FCSTD DOCUMENT  (FreeCAD 0.15R4671 (Git))
Label: plate
License: All rights reserved
LicenseURL: http://en.wikipedia.org/wiki/All_rights_reserved
objects: Sketcher::SketchObject×1
note: 1 computed .brp shape members not serialized (recipe doc carries the construction recipe); baked Part::Feature solids carry a one-line shape summary decoded from their .brp

FEATURE [Sketcher::SketchObject] Sketch
  sketch-geometry (29):
    g0: Circle [constr] CenterX=0 CenterY=0 CenterZ=0 NormalX=0 NormalY=0 NormalZ=1 Radius=72.75
    g1: Circle [constr] CenterX=0 CenterY=0 CenterZ=0 NormalX=0 NormalY=0 NormalZ=1 Radius=99.75
    g2: LineSegment [constr] StartX=-72.75 StartY=0 StartZ=0 EndX=-99.75 EndY=0 EndZ=0
    g3: Circle [constr] CenterX=0 CenterY=0 CenterZ=0 NormalX=0 NormalY=0 NormalZ=1 Radius=79.25
    g4: LineSegment [constr] StartX=72.75 StartY=0 StartZ=0 EndX=79.25 EndY=0 EndZ=0
    g5: Circle [constr] CenterX=0 CenterY=0 CenterZ=0 NormalX=0 NormalY=0 NormalZ=1 Radius=93.25
    g6: LineSegment [constr] StartX=93.25 StartY=0 StartZ=0 EndX=99.75 EndY=0 EndZ=0
    g7: LineSegment [constr] StartX=0 StartY=0 StartZ=0 EndX=0 EndY=200 EndZ=0
    g8: LineSegment [constr] StartX=0 StartY=0 StartZ=0 EndX=0 EndY=-200 EndZ=0
    g9: Circle CenterX=0 CenterY=93.25 CenterZ=0 NormalX=0 NormalY=0 NormalZ=1 Radius=4.75
    g10: Circle CenterX=93.25 CenterY=0 CenterZ=0 NormalX=0 NormalY=0 NormalZ=1 Radius=4.75
    g11: Circle CenterX=-93.25 CenterY=0 CenterZ=0 NormalX=0 NormalY=0 NormalZ=1 Radius=4.75
    g12: Circle CenterX=0 CenterY=-93.25 CenterZ=0 NormalX=0 NormalY=0 NormalZ=1 Radius=4.75
    g13: Circle CenterX=0 CenterY=0 CenterZ=0 NormalX=0 NormalY=0 NormalZ=1 Radius=102
    g14: Circle [constr] CenterX=0 CenterY=0 CenterZ=0 NormalX=0 NormalY=0 NormalZ=1 Radius=64.935
    g15: Circle [constr] CenterX=0 CenterY=40.745 CenterZ=0 NormalX=0 NormalY=0 NormalZ=1 Radius=24.19
    g16: Circle CenterX=0 CenterY=40.745 CenterZ=0 NormalX=0 NormalY=0 NormalZ=1 Radius=9
    g17: LineSegment [constr] StartX=-29.7982 StartY=48.145 StartZ=0 EndX=0 EndY=48.145 EndZ=0
    g18: Circle CenterX=-17.45 CenterY=48.145 CenterZ=0 NormalX=0 NormalY=0 NormalZ=1 Radius=2
    g19: Circle CenterX=17.45 CenterY=48.145 CenterZ=0 NormalX=0 NormalY=0 NormalZ=1 Radius=2
    g20: LineSegment [constr] StartX=0 StartY=40.745 StartZ=0 EndX=0 EndY=48.145 EndZ=0
    g21: Circle [constr] CenterX=0 CenterY=0 CenterZ=0 NormalX=0 NormalY=0 NormalZ=1 Radius=17.25
    g22: Circle [constr] CenterX=0 CenterY=0 CenterZ=0 NormalX=0 NormalY=0 NormalZ=1 Radius=22.25
    g23: LineSegment [constr] StartX=0 StartY=0 StartZ=0 EndX=38.1051 EndY=22 EndZ=0
    g24: LineSegment [constr] StartX=0 StartY=0 StartZ=0 EndX=-38.1051 EndY=22 EndZ=0
    g25: Circle CenterX=0 CenterY=0 CenterZ=0 NormalX=0 NormalY=0 NormalZ=1 Radius=11.25
    g26: Circle CenterX=0 CenterY=-17.25 CenterZ=0 NormalX=0 NormalY=0 NormalZ=1 Radius=3
    g27: Circle CenterX=14.9389 CenterY=8.625 CenterZ=0 NormalX=0 NormalY=0 NormalZ=1 Radius=3
    g28: Circle CenterX=-14.9389 CenterY=8.625 CenterZ=0 NormalX=0 NormalY=0 NormalZ=1 Radius=3
  constraints (79):
    c: Radius(g0) = 72.75
    c: PointOnObject(g2,g0)
    c: PointOnObject(g2,g1)
    c: PointOnObject(g2,g-1)
    c: PointOnObject(g2,g-1)
    c: Distance(g2) = 27
    c: PointOnObject(g4,g0)
    c: PointOnObject(g4,g3)
    c: PointOnObject(g4,g-1)
    c: PointOnObject(g4,g-1)
    c: Distance(g4) = 6.5
    c: PointOnObject(g6,g5)
    c: PointOnObject(g6,g1)
    c: PointOnObject(g6,g-1)
    c: PointOnObject(g6,g-1)
    c: Distance(g6) = 6.5
    c: Coincident(g7,g-1)
    c: Vertical(g7)
    c: Distance(g7) = 200
    c: Coincident(g8,g-1)
    c: Vertical(g8)
    c: Distance(g8) = 200
    c: Coincident(g3,g-1)
    c: Coincident(g-1,g1)
    c: Coincident(g0,g-1)
    c: PointOnObject(g9,g5)
    c: PointOnObject(g9,g7)
    c: Radius(g9) = 4.75
    c: PointOnObject(g10,g5)
    c: Equal(g10,g9)
    c: PointOnObject(g10,g-1)
    c: PointOnObject(g11,g2)
    c: Equal(g11,g9)
    c: PointOnObject(g11,g5)
    c: Coincident(g5,g-1)
    c: PointOnObject(g12,g8)
    c: Equal(g12,g10)
    c: PointOnObject(g12,g5)
    c: Coincident(g13,g-1)
    c: Radius(g13) = 102
    c: Coincident(g14,g-1)
    c: Radius(g14) = 64.935
    c: Radius(g15) = 24.19
    c: Tangent(g15,g14)
    c: PointOnObject(g15,g7)
    c: Coincident(g16,g15)
    c: Radius(g16) = 9
    c: Horizontal(g17)
    c: Distance(g17) = 29.7982
    c: PointOnObject(g18,g17)
    c: Equal(g18,g19)
    c: Symmetric(g18,g19,g7)
    c: DistanceX(g18) = -17.45
    c: Radius(g18) = 2
    c: PointOnObject(g17,g7)
    c: Coincident(g20,g15)
    c: Coincident(g20,g17)
    c: Coincident(g21,g-1)
    c: Radius(g21) = 17.25
    c: Coincident(g22,g-1)
    c: Radius(g22) = 22.25
    c: Distance(g20) = 7.4
    c: Coincident(g23,g-1)
    c: Distance(g23) = 44
    c: Angle(g8,g23) = 2.0944
    c: Coincident(g24,g-1)
    c: Distance(g24) = 44
    c: Angle(g24,g8) = 2.0944
    c: Coincident(g25,g-1)
    c: Radius(g25) = 11.25
    c: Radius(g26) = 3
    c: PointOnObject(g26,g8)
    c: PointOnObject(g26,g21)
    c: PointOnObject(g27,g23)
    c: PointOnObject(g28,g24)
    c: Equal(g26,g27)
    c: Equal(g27,g28)
    c: PointOnObject(g27,g21)
    c: PointOnObject(g28,g21)
